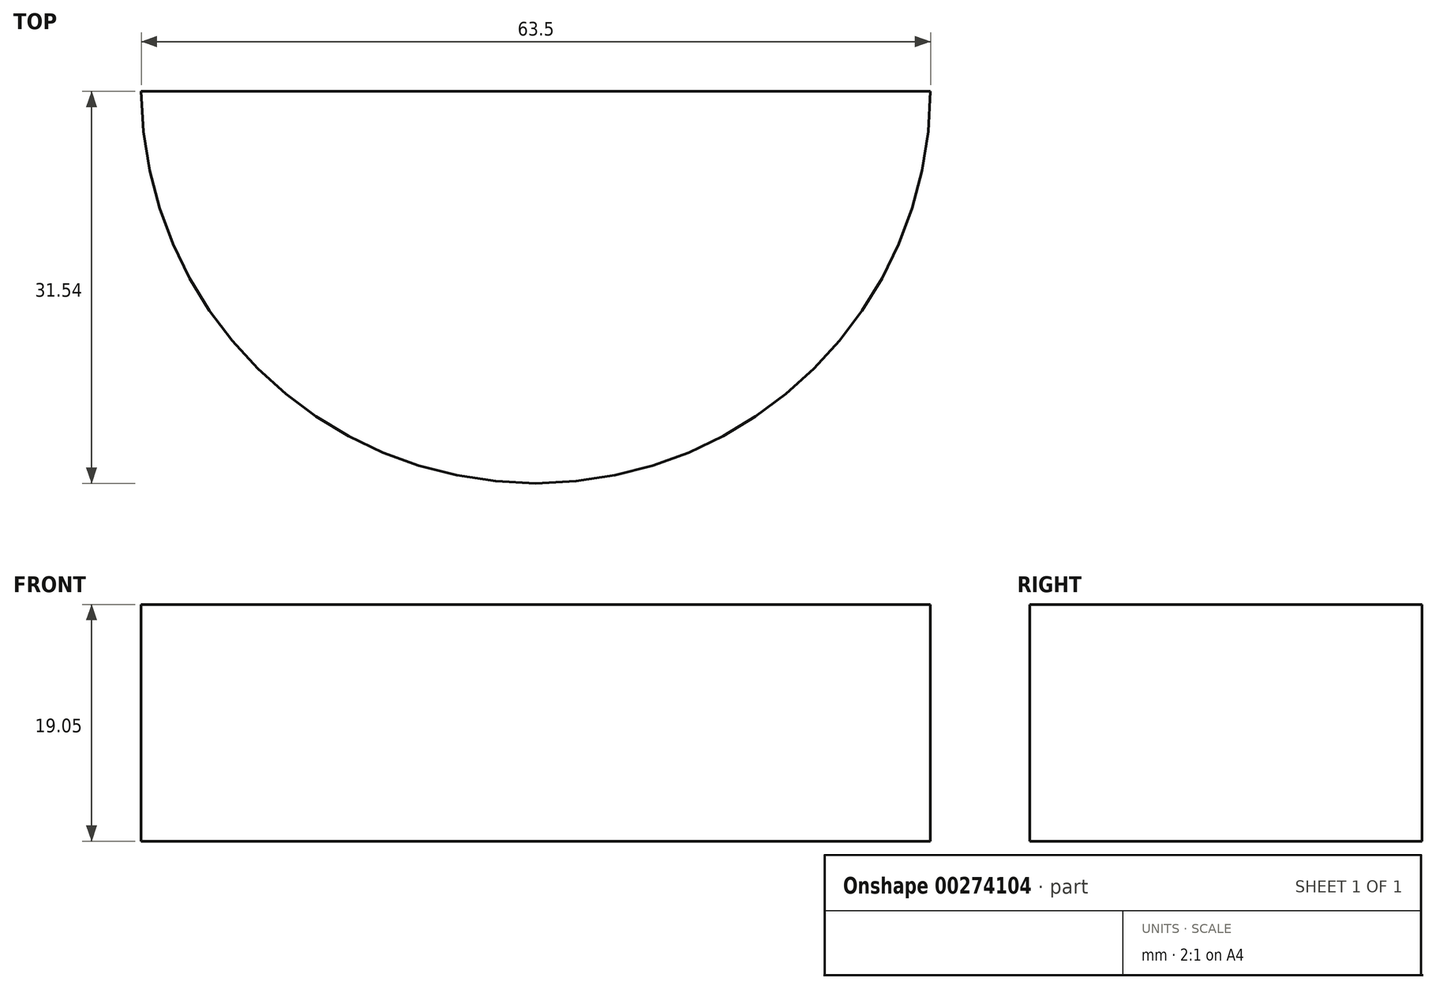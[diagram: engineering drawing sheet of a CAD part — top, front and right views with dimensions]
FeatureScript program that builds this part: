
annotation { "Feature Type Name" : "Feature", "Feature Type Description" : "" }
export const myFeature = defineFeature(function(context is Context, id is Id, definition is map)
    precondition{}
    {
        {
            var Q0;
            Q0=qCreatedBy(makeId("Top.planeOp"),FACE);
            var sketch = newSketch(context, id + "F0", { "sketchPlane" : qUnion([Q0])});
            skArc(sketch, "E0", {"start": v(-32.84, 0) * mm, "mid": v(-1.1, -31.54) * mm, "end": v(30.66, 0) * mm});
            skLineSegment(sketch, "E1", {"start": v(-32.84, 0) * mm, "end": v(30.66, 0) * mm});
            skSolve(sketch);
        }
        {
            var Q0;
            Q0 = qSketchRegion(id + "F0", true);
            extrude(context, id + "F1", {"entities" : qUnion([Q0]), "depth" : 19.05 * mm});
        }
    });
